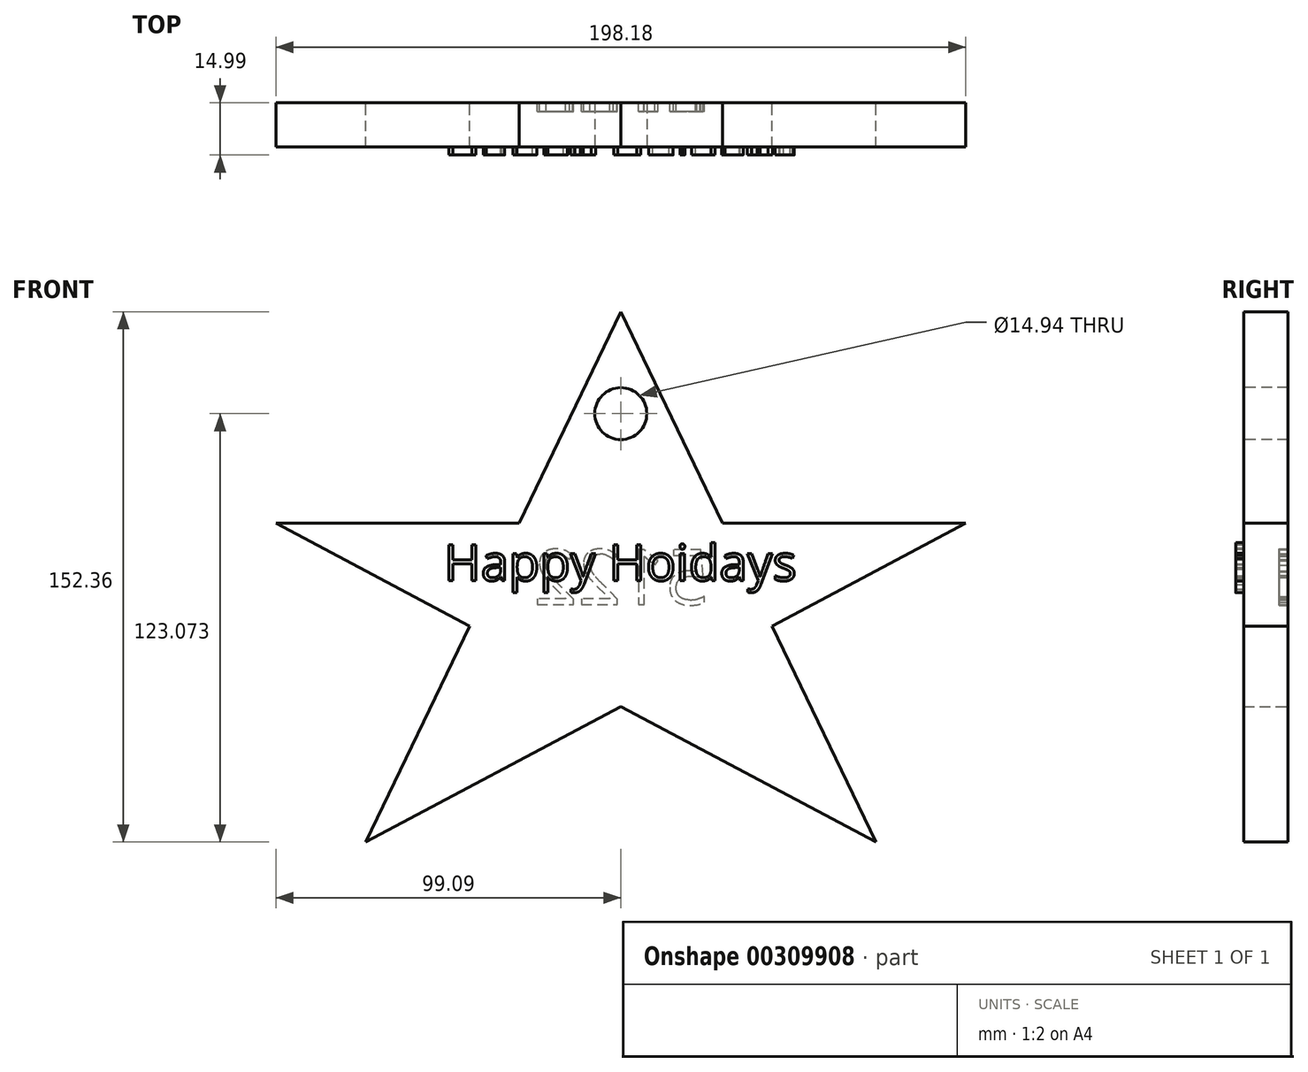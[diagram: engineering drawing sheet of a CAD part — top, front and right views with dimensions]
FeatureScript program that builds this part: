
annotation { "Feature Type Name" : "Feature", "Feature Type Description" : "" }
export const myFeature = defineFeature(function(context is Context, id is Id, definition is map)
    precondition{}
    {
        {
            var Q0;
            Q0=qCreatedBy(makeId("Front.planeOp"),FACE);
            var sketch = newSketch(context, id + "F0", { "sketchPlane" : qUnion([Q0])});
            skLineSegment(sketch, "E0", {"start": v(-73.31, -73.68) * mm, "end": v(-43.46, -11.65) * mm});
            skLineSegment(sketch, "E1", {"start": v(0, 78.68) * mm, "end": v(29.24, 17.9) * mm});
            skLineSegment(sketch, "E2", {"start": v(73.31, -73.67) * mm, "end": v(0, -34.73) * mm});
            skLineSegment(sketch, "E3", {"start": v(-99.1, 17.9) * mm, "end": v(-29.24, 17.9) * mm});
            skLineSegment(sketch, "E4", {"start": v(99.1, 17.9) * mm, "end": v(43.46, -11.65) * mm});
            skLineSegment(sketch, "E5.trimOffspring", {"start": v(29.24, 17.9) * mm, "end": v(99.1, 17.9) * mm});
            skLineSegment(sketch, "E6.trimOffspring", {"start": v(-29.24, 17.9) * mm, "end": v(0, 78.68) * mm});
            skLineSegment(sketch, "E7.trimOffspring", {"start": v(-43.46, -11.65) * mm, "end": v(-99.1, 17.9) * mm});
            skLineSegment(sketch, "E8.trimOffspring", {"start": v(0, -34.73) * mm, "end": v(-73.31, -73.68) * mm});
            skLineSegment(sketch, "E9.trimOffspring", {"start": v(43.46, -11.65) * mm, "end": v(73.31, -73.67) * mm});
            skSolve(sketch);
        }
        {
            var Q0;
            Q0 = qSketchRegion(id + "F0", true);
            extrude(context, id + "F1", {"entities" : qUnion([Q0]), "depth" : 12.7 * mm});
        }
        {
            var Q0;
            Q0=makeQuery(id+"F1.opExtrude","CAP_FACE",FACE,{"disambiguationData":[OSD([sQuery(id+"F0.wireOp",EDGE,"E0"),sQuery(id+"F0.wireOp",EDGE,"E1"),sQuery(id+"F0.wireOp",EDGE,"E2"),sQuery(id+"F0.wireOp",EDGE,"E3"),sQuery(id+"F0.wireOp",EDGE,"E4"),sQuery(id+"F0.wireOp",EDGE,"E5.trimOffspring"),sQuery(id+"F0.wireOp",EDGE,"E6.trimOffspring"),sQuery(id+"F0.wireOp",EDGE,"E7.trimOffspring"),sQuery(id+"F0.wireOp",EDGE,"E8.trimOffspring"),sQuery(id+"F0.wireOp",EDGE,"E9.trimOffspring")])],"isStart":false});
            var sketch = newSketch(context, id + "F2", { "sketchPlane" : qUnion([Q0])});
            skCircle(sketch, "E10", {"center": v(0, 49.4) * mm, "radius": 7.47 * mm});
            skSolve(sketch);
        }
        {
            var Q0;
            Q0 = qSketchRegion(id + "F2", true);
            extrude(context, id + "F3", {"entities" : qUnion([Q0]), "operationType" : NewBodyOperationType.REMOVE, "oppositeDirection" : true, "depth" : 25.4 * mm});
        }
        {
            var Q0;
            Q0=makeQuery(id+"F1.opExtrude","CAP_FACE",FACE,{"disambiguationData":[OSD([sQuery(id+"F0.wireOp",EDGE,"E0"),sQuery(id+"F0.wireOp",EDGE,"E1"),sQuery(id+"F0.wireOp",EDGE,"E2"),sQuery(id+"F0.wireOp",EDGE,"E3"),sQuery(id+"F0.wireOp",EDGE,"E4"),sQuery(id+"F0.wireOp",EDGE,"E5.trimOffspring"),sQuery(id+"F0.wireOp",EDGE,"E6.trimOffspring"),sQuery(id+"F0.wireOp",EDGE,"E7.trimOffspring"),sQuery(id+"F0.wireOp",EDGE,"E8.trimOffspring"),sQuery(id+"F0.wireOp",EDGE,"E9.trimOffspring")])],"isStart":false});
            var sketch = newSketch(context, id + "F4", { "sketchPlane" : qUnion([Q0])});
            skCircle(sketch, "E11", {"center": v(0, 48.25) * mm, "radius": 7.65 * mm});
            skSolve(sketch);
        }
        {
            var Q0;
            Q0=makeQuery(id+"F4.imprint","IMPRINT",FACE,{"disambiguationData":[TD([[makeQuery(id+"F4.imprint","IMPRINT",EDGE,{"derivedFrom":makeQuery(id+"F1.opExtrude","CAP_EDGE",EDGE,{"disambiguationData":[OSD([sQuery(id+"F0.wireOp",EDGE,"E0")])],"isStart":false})}),-1.0]])]});
            var sketch = newSketch(context, id + "F5", { "sketchPlane" : qUnion([Q0])});
            skText(sketch, "E12", { "text": "Happy Hoidays", "fontName": "OpenSans-Regular.ttf"});
            const initialGuessF5  = {"E12": [-0.05083, 0.00143, 1, 0, 0.01038]};
            skSetInitialGuess(sketch, initialGuessF5);
            skSolve(sketch);
        }
        {
            var Q0;
            Q0 = qSketchRegion(id + "F5", true);
            extrude(context, id + "F6", {"entities" : qUnion([Q0]), "operationType" : NewBodyOperationType.ADD, "depth" : 2.3 * mm});
        }
        {
            var Q0;
            Q0=makeQuery(id+"F1.opExtrude","CAP_FACE",FACE,{"disambiguationData":[OSD([sQuery(id+"F0.wireOp",EDGE,"E0"),sQuery(id+"F0.wireOp",EDGE,"E1"),sQuery(id+"F0.wireOp",EDGE,"E2"),sQuery(id+"F0.wireOp",EDGE,"E3"),sQuery(id+"F0.wireOp",EDGE,"E4"),sQuery(id+"F0.wireOp",EDGE,"E5.trimOffspring"),sQuery(id+"F0.wireOp",EDGE,"E6.trimOffspring"),sQuery(id+"F0.wireOp",EDGE,"E7.trimOffspring"),sQuery(id+"F0.wireOp",EDGE,"E8.trimOffspring"),sQuery(id+"F0.wireOp",EDGE,"E9.trimOffspring")])],"isStart":true});
            var sketch = newSketch(context, id + "F7", { "sketchPlane" : qUnion([Q0])});
            skText(sketch, "E13", { "text": "5122", "fontName": "OpenSans-Regular.ttf"});
            const initialGuessF7  = {"E13": [-0.02543, -0.00545, 1, 0, 0.01594]};
            skSetInitialGuess(sketch, initialGuessF7);
            skSolve(sketch);
        }
        {
            var Q0;
            Q0 = qSketchRegion(id + "F7", true);
            extrude(context, id + "F8", {"entities" : qUnion([Q0]), "operationType" : NewBodyOperationType.REMOVE, "oppositeDirection" : true, "depth" : 2.54 * mm});
        }
    });
